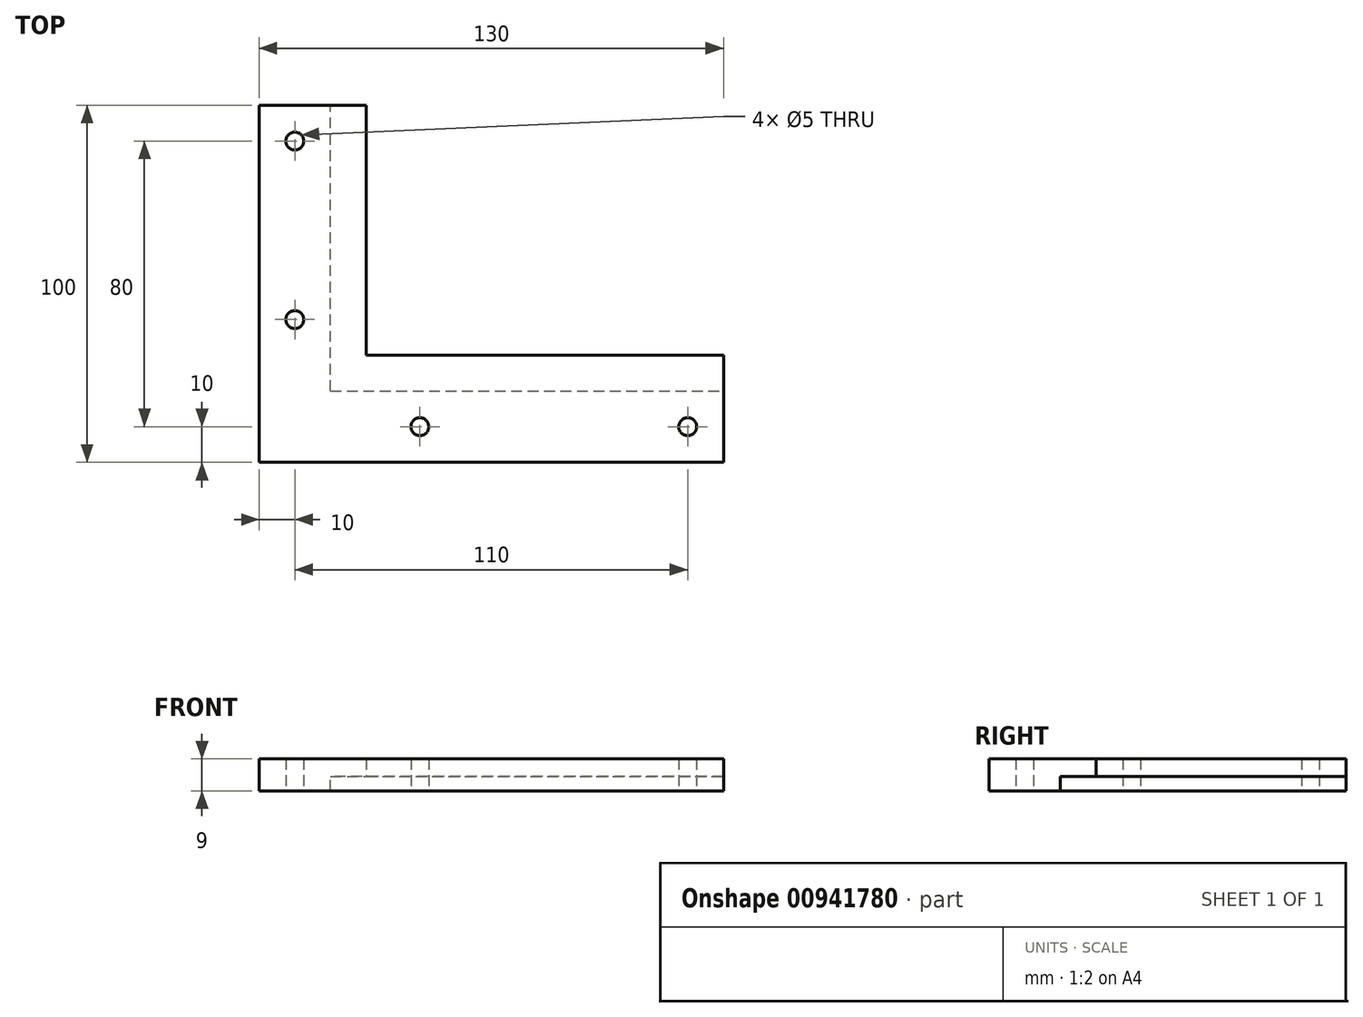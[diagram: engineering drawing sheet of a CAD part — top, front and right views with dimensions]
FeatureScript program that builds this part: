
annotation { "Feature Type Name" : "Feature", "Feature Type Description" : "" }
export const myFeature = defineFeature(function(context is Context, id is Id, definition is map)
    precondition{}
    {
        {
            var Q0;
            Q0=qCreatedBy(makeId("Top.planeOp"),FACE);
            var sketch = newSketch(context, id + "F0", { "sketchPlane" : qUnion([Q0])});
            skEllipticalArc(sketch, "E0", {});
            skLineSegment(sketch, "E1", {"start": v(-116.5, 0) * mm, "end": v(-116.5, -86.5) * mm});
            skPoint(sketch, "E1.endSnap0", {"position": v(0, -86.5) * mm});
            skLineSegment(sketch, "E2", {"start": v(-116.5, -86.5) * mm, "end": v(0, -86.5) * mm});
            skLineSegment(sketch, "E3", {"start": v(-116.5, 0) * mm, "end": v(-130, 0) * mm});
            skLineSegment(sketch, "E4", {"start": v(-130, 0) * mm, "end": v(-130, -100) * mm});
            skLineSegment(sketch, "E5", {"start": v(-130, -100) * mm, "end": v(0, -100) * mm});
            skLineSegment(sketch, "E6", {"start": v(0, -100) * mm, "end": v(0, -86.5) * mm});
            const initialGuessF0  = {"E0": [0, 0, 1, 0, 0.1165, 0.0865, 3.141592653589793, 4.71238898038469]};
            skSetInitialGuess(sketch, initialGuessF0);
            skSolve(sketch);
        }
        {
            var Q0;
            Q0=qSketchRegion(id+"F0",true);
            extrude(context, id + "F1", {"entities" : qUnion([Q0]), "depth" : 12 * mm, "offsetDistance" : 25 * mm});
        }
        {
            var Q0;
            Q0=makeQuery(id+"F1.opExtrude","SWEPT_FACE",FACE,{"disambiguationData":[OSD([sQuery(id+"F0.wireOp",EDGE,"E5")])]});
            var sketch = newSketch(context, id + "F2", { "sketchPlane" : qUnion([Q0])});
            skLineSegment(sketch, "E7.bottom", {"start": v(-130, 16) * mm, "end": v(0, 16) * mm});
            skLineSegment(sketch, "E7.top", {"start": v(-130, -4) * mm, "end": v(0, -4) * mm});
            skLineSegment(sketch, "E7.left", {"start": v(-130, 16) * mm, "end": v(-130, -4) * mm});
            skLineSegment(sketch, "E7.right", {"start": v(0, 16) * mm, "end": v(0, -4) * mm});
            skSolve(sketch);
        }
        {
            var Q0;
            Q0=qSketchRegion(id+"F2",true);
            extrude(context, id + "F3", {"entities" : qUnion([Q0]), "operationType" : NewBodyOperationType.ADD, "depth" : 5 * mm, "offsetDistance" : 25 * mm});
        }
        {
            var Q0;
            Q0=makeQuery(id+"F3.boolean.opBoolean","MERGE",FACE,{"derivedFrom":[makeQuery(id+"F1.opExtrude","SWEPT_FACE",FACE,{"disambiguationData":[OSD([sQuery(id+"F0.wireOp",EDGE,"E4")])]}),makeQuery(id+"F3.opExtrude","SWEPT_FACE",FACE,{"disambiguationData":[OSD([sQuery(id+"F2.wireOp",EDGE,"E7.left")])]})]});
            var sketch = newSketch(context, id + "F4", { "sketchPlane" : qUnion([Q0])});
            skLineSegment(sketch, "E8.bottom", {"start": v(105, 16) * mm, "end": v(0, 16) * mm});
            skLineSegment(sketch, "E8.top", {"start": v(105, -4) * mm, "end": v(0, -4) * mm});
            skLineSegment(sketch, "E8.left", {"start": v(105, 16) * mm, "end": v(105, -4) * mm});
            skLineSegment(sketch, "E8.right", {"start": v(0, 16) * mm, "end": v(0, -4) * mm});
            skSolve(sketch);
        }
        {
            var Q0;
            Q0=qSketchRegion(id+"F4",true);
            extrude(context, id + "F5", {"entities" : qUnion([Q0]), "operationType" : NewBodyOperationType.ADD, "depth" : 5 * mm, "offsetDistance" : 25 * mm});
        }
        {
            var Q0;
            Q0=makeQuery(id+"F5.boolean.opBoolean","MERGE",FACE,{"derivedFrom":[makeQuery(id+"F3.opExtrude","SWEPT_FACE",FACE,{"disambiguationData":[OSD([sQuery(id+"F2.wireOp",EDGE,"E7.bottom")])]}),makeQuery(id+"F5.opExtrude","SWEPT_FACE",FACE,{"disambiguationData":[OSD([sQuery(id+"F4.wireOp",EDGE,"E8.bottom")])]})]});
            var sketch = newSketch(context, id + "F6", { "sketchPlane" : qUnion([Q0])});
            skLineSegment(sketch, "E9", {"start": v(-135, 0) * mm, "end": v(-120, 0) * mm});
            skLineSegment(sketch, "E10", {"start": v(-120, 0) * mm, "end": v(-120, -90) * mm});
            skLineSegment(sketch, "E11", {"start": v(-120, -90) * mm, "end": v(0, -90) * mm});
            skLineSegment(sketch, "E12", {"start": v(0, -90) * mm, "end": v(0, -105) * mm});
            skLineSegment(sketch, "E13", {"start": v(0, -105) * mm, "end": v(-135, -105) * mm});
            skLineSegment(sketch, "E14", {"start": v(-135, -105) * mm, "end": v(-135, 0) * mm});
            skSolve(sketch);
        }
        {
            var Q0;
            Q0=makeQuery(id+"F5.boolean.opBoolean","MERGE",FACE,{"derivedFrom":[makeQuery(id+"F3.opExtrude","SWEPT_FACE",FACE,{"disambiguationData":[OSD([sQuery(id+"F2.wireOp",EDGE,"E7.top")])]}),makeQuery(id+"F5.opExtrude","SWEPT_FACE",FACE,{"disambiguationData":[OSD([sQuery(id+"F4.wireOp",EDGE,"E8.top")])]})]});
            var sketch = newSketch(context, id + "F7", { "sketchPlane" : qUnion([Q0])});
            skLineSegment(sketch, "E15.bottom", {"start": v(-130, 0) * mm, "end": v(-150, 0) * mm});
            skLineSegment(sketch, "E15.top", {"start": v(-130, 120) * mm, "end": v(-150, 120) * mm});
            skLineSegment(sketch, "E15.left", {"start": v(-130, 0) * mm, "end": v(-130, 120) * mm});
            skLineSegment(sketch, "E15.right", {"start": v(-150, 0) * mm, "end": v(-150, 120) * mm});
            skLineSegment(sketch, "E16.bottom", {"start": v(0, 100) * mm, "end": v(-150, 100) * mm});
            skLineSegment(sketch, "E16.top", {"start": v(0, 120) * mm, "end": v(-150, 120) * mm});
            skLineSegment(sketch, "E16.left", {"start": v(0, 100) * mm, "end": v(0, 120) * mm});
            skLineSegment(sketch, "E16.right", {"start": v(-150, 100) * mm, "end": v(-150, 120) * mm});
            skCircle(sketch, "E17", {"center": v(-140, 30) * mm, "radius": 2.5 * mm});
            skCircle(sketch, "E18", {"center": v(-140, 80) * mm, "radius": 2.5 * mm});
            skCircle(sketch, "E19", {"center": v(-105, 110) * mm, "radius": 2.5 * mm});
            skCircle(sketch, "E20", {"center": v(-30, 110) * mm, "radius": 2.5 * mm});
            skSolve(sketch);
        }
        {
            var Q0;
            Q0=qSketchRegion(id+"F7",true);
            extrude(context, id + "F8", {"entities" : qUnion([Q0]), "operationType" : NewBodyOperationType.ADD, "oppositeDirection" : true, "depth" : 25 * mm, "offsetDistance" : 25 * mm});
        }
        {
            var Q0;
            Q0=qSketchRegion(id+"F6",true);
            extrude(context, id + "F9", {"entities" : qUnion([Q0]), "operationType" : NewBodyOperationType.ADD, "depth" : 5 * mm, "offsetDistance" : 25 * mm});
        }
        {
            var Q0;
            Q0=qCreatedBy(makeId("Top.planeOp"),FACE);
            var sketch = newSketch(context, id + "F10", { "sketchPlane" : qUnion([Q0])});
            skLineSegment(sketch, "E21.bottom", {"start": v(-150, 0) * mm, "end": v(0, 0) * mm});
            skLineSegment(sketch, "E21.top", {"start": v(-150, -20) * mm, "end": v(0, -20) * mm});
            skLineSegment(sketch, "E21.left", {"start": v(-150, 0) * mm, "end": v(-150, -20) * mm});
            skLineSegment(sketch, "E21.right", {"start": v(0, 0) * mm, "end": v(0, -20) * mm});
            skLineSegment(sketch, "E22.bottom", {"start": v(0, -120) * mm, "end": v(-20, -120) * mm});
            skLineSegment(sketch, "E22.top", {"start": v(0, 0) * mm, "end": v(-20, 0) * mm});
            skLineSegment(sketch, "E22.left", {"start": v(0, -120) * mm, "end": v(0, 0) * mm});
            skLineSegment(sketch, "E22.right", {"start": v(-20, -120) * mm, "end": v(-20, 0) * mm});
            skSolve(sketch);
        }
        {
            var Q0;
            Q0=qSketchRegion(id+"F10",true);
            extrude(context, id + "F11", {"entities" : qUnion([Q0]), "operationType" : NewBodyOperationType.REMOVE, "endBound" : BoundingType.SYMMETRIC, "oppositeDirection" : true, "depth" : 50 * mm, "offsetDistance" : 25 * mm});
        }
        {
            var Q0;
            Q0=makeQuery(id+"F11.boolean.opBoolean","COPY",FACE,{"derivedFrom":makeQuery(id+"F11.opExtrude","SWEPT_FACE",FACE,{"disambiguationData":[OSD([sQuery(id+"F10.wireOp",EDGE,"E22.right")])]})});
            var sketch = newSketch(context, id + "F12", { "sketchPlane" : qUnion([Q0])});
            skPoint(sketch, "E23.oppositeSnap0", {"position": v(-92.6, 12) * mm});
            skLineSegment(sketch, "E23.bottom", {"start": v(-120, -4) * mm, "end": v(-20, -4) * mm});
            skLineSegment(sketch, "E23.top", {"start": v(-120, 12) * mm, "end": v(-20, 12) * mm});
            skLineSegment(sketch, "E23.left", {"start": v(-120, -4) * mm, "end": v(-120, 12) * mm});
            skLineSegment(sketch, "E23.right", {"start": v(-20, -4) * mm, "end": v(-20, 12) * mm});
            skSolve(sketch);
        }
        {
            var Q0;
            Q0 = qSketchRegion(id + "F12", true);
            extrude(context, id + "F13", {"entities" : qUnion([Q0]), "operationType" : NewBodyOperationType.REMOVE, "oppositeDirection" : true, "depth" : 150 * mm, "offsetDistance" : 25 * mm});
        }
    });
